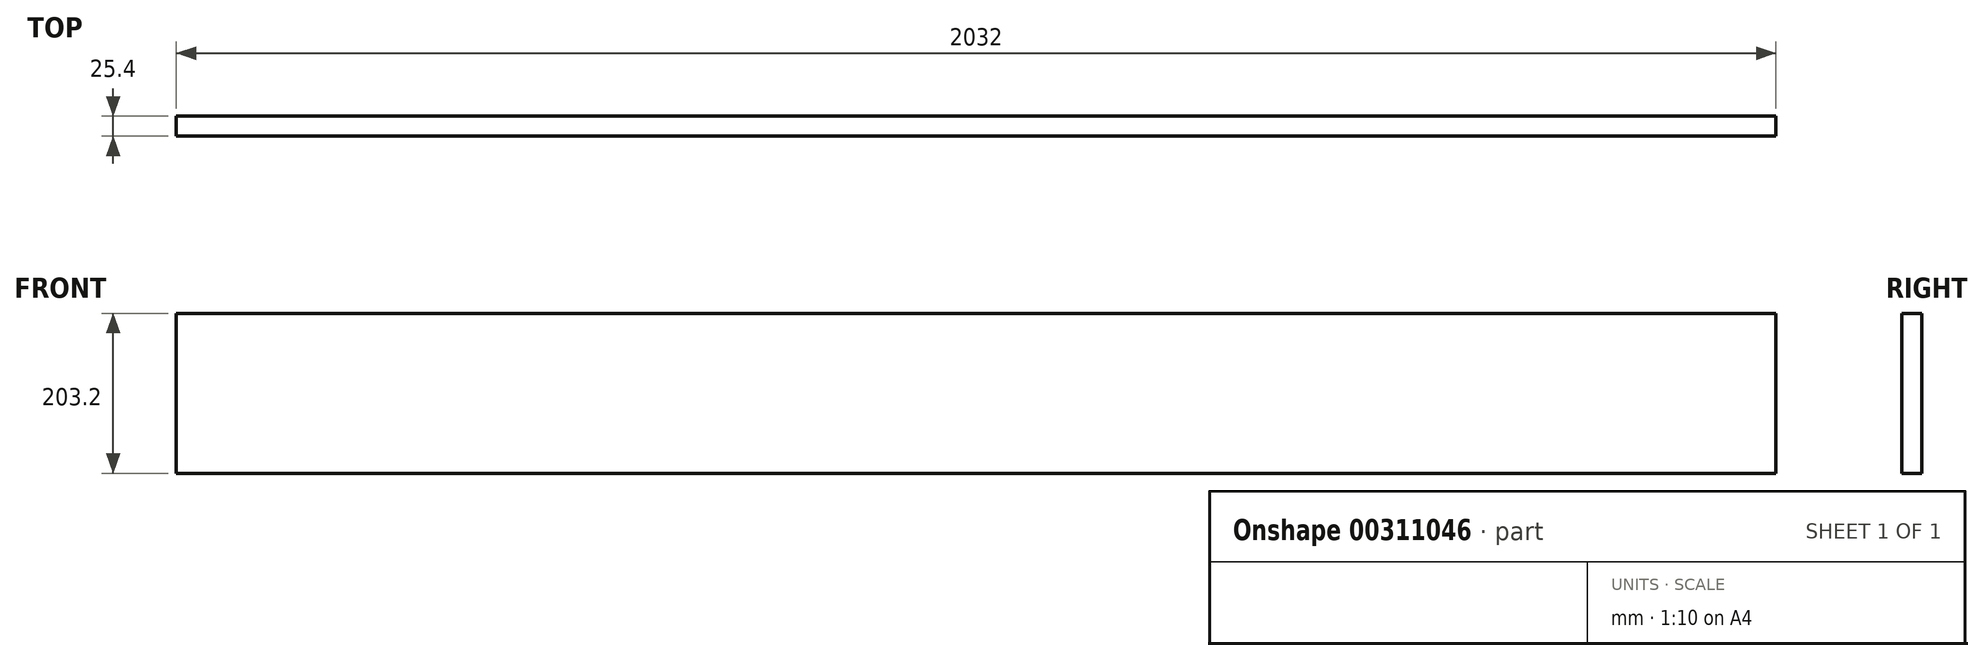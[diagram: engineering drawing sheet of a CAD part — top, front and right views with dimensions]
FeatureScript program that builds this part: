
annotation { "Feature Type Name" : "Feature", "Feature Type Description" : "" }
export const myFeature = defineFeature(function(context is Context, id is Id, definition is map)
    precondition{}
    {
        {
            var Q0;
            Q0=qCreatedBy(makeId("Front.planeOp"),FACE);
            var sketch = newSketch(context, id + "F0", { "sketchPlane" : qUnion([Q0])});
            skLineSegment(sketch, "E0.bottom", {"start": v(-128.18, 203.2) * mm, "end": v(1903.82, 203.2) * mm});
            skLineSegment(sketch, "E0.top", {"start": v(-128.18, 0) * mm, "end": v(1903.82, 0) * mm});
            skLineSegment(sketch, "E0.left", {"start": v(-128.18, 203.2) * mm, "end": v(-128.18, 0) * mm});
            skLineSegment(sketch, "E0.right", {"start": v(1903.82, 203.2) * mm, "end": v(1903.82, 0) * mm});
            skSolve(sketch);
        }
        {
            var Q0;
            Q0 = qSketchRegion(id + "F0", true);
            extrude(context, id + "F1", {"entities" : qUnion([Q0]), "depth" : 25.4 * mm});
        }
    });
